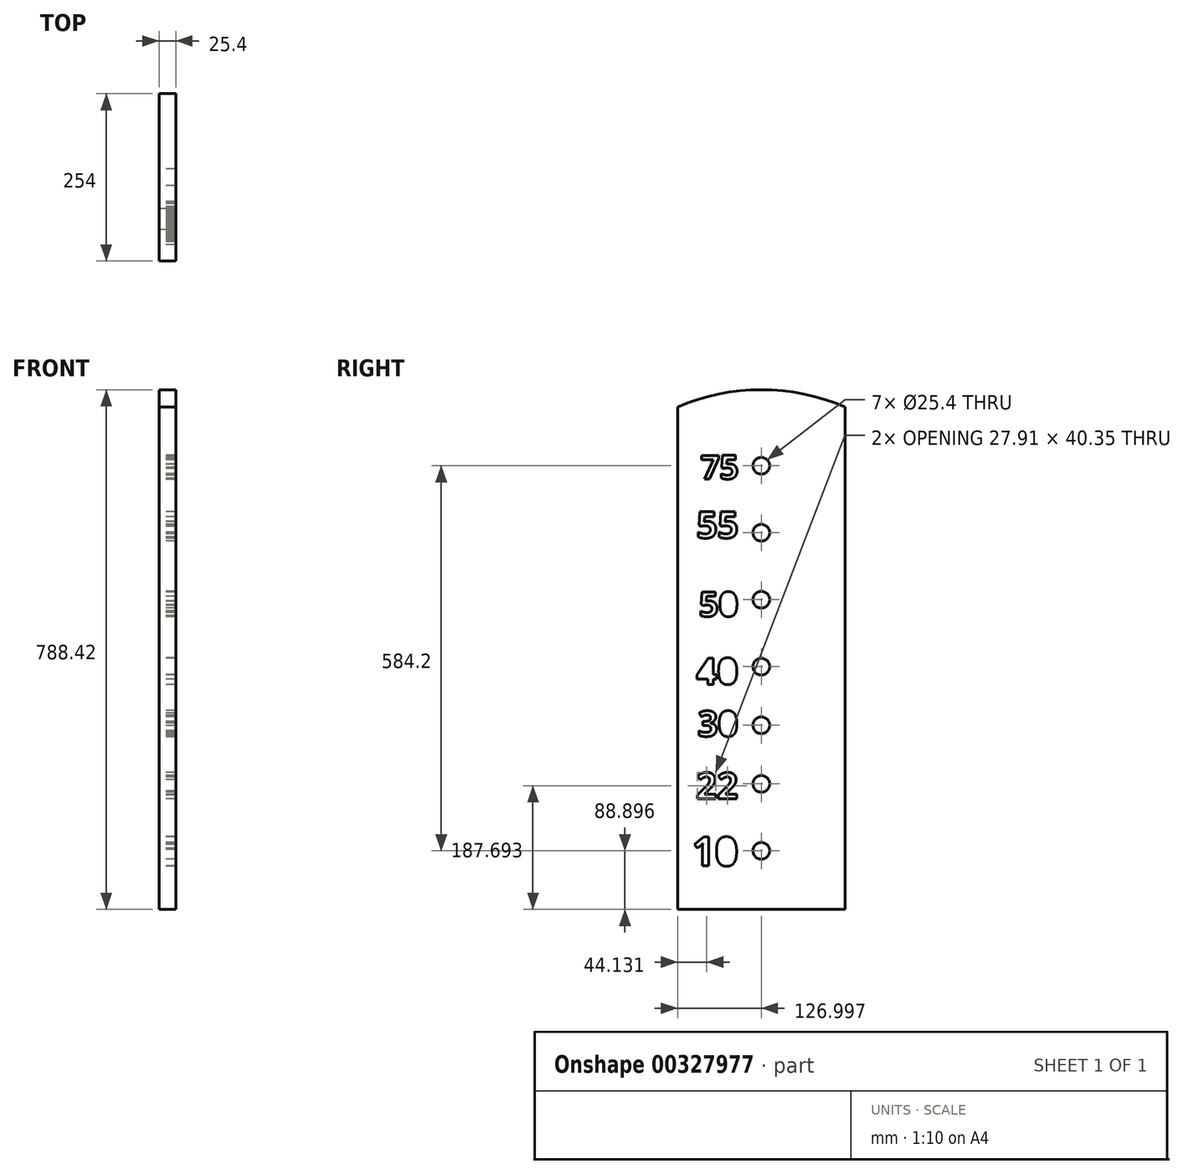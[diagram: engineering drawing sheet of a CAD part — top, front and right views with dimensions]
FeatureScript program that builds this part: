
annotation { "Feature Type Name" : "Feature", "Feature Type Description" : "" }
export const myFeature = defineFeature(function(context is Context, id is Id, definition is map)
    precondition{}
    {
        {
            var Q0;
            Q0=qCreatedBy(makeId("Right.planeOp"),FACE);
            var sketch = newSketch(context, id + "F0", { "sketchPlane" : qUnion([Q0])});
            skArc(sketch, "E0", {"start": v(-63.95, 233.67) * mm, "mid": v(-190.95, 260.09) * mm, "end": v(-317.95, 233.67) * mm});
            skLineSegment(sketch, "E1", {"start": v(-317.95, 233.67) * mm, "end": v(-317.95, -528.33) * mm});
            skLineSegment(sketch, "E2", {"start": v(-63.95, 233.67) * mm, "end": v(-63.95, -528.33) * mm});
            skLineSegment(sketch, "E3", {"start": v(-63.95, -528.33) * mm, "end": v(-317.95, -528.33) * mm});
            skCircle(sketch, "E4", {"center": v(-190.95, -439.43) * mm, "radius": 12.7 * mm});
            skPoint(sketch, "E4.centerSnap0", {"position": v(-190.95, -528.33) * mm});
            skCircle(sketch, "E5", {"center": v(-190.95, -337.83) * mm, "radius": 12.7 * mm});
            skCircle(sketch, "E6", {"center": v(-190.95, -248.93) * mm, "radius": 12.7 * mm});
            skCircle(sketch, "E7", {"center": v(-190.95, -160.03) * mm, "radius": 12.7 * mm});
            skCircle(sketch, "E8", {"center": v(-190.95, -58.43) * mm, "radius": 12.7 * mm});
            skCircle(sketch, "E9", {"center": v(-190.95, 43.17) * mm, "radius": 12.7 * mm});
            skCircle(sketch, "E10", {"center": v(-190.95, 144.77) * mm, "radius": 12.7 * mm});
            skText(sketch, "E11", { "text": "75", "fontName": "OpenSans-Bold.ttf"});
            skText(sketch, "E12", { "text": "55", "fontName": "OpenSans-Bold.ttf"});
            skPoint(sketch, "E12.secondSnap0", {"position": v(-224.45, 142.71) * mm});
            skText(sketch, "E13", { "text": "50", "fontName": "OpenSans-Bold.ttf"});
            skText(sketch, "E14", { "text": "40", "fontName": "OpenSans-Bold.ttf"});
            skText(sketch, "E15", { "text": "30", "fontName": "OpenSans-Bold.ttf"});
            skText(sketch, "E16", { "text": "22", "fontName": "OpenSans-Bold.ttf"});
            skText(sketch, "E17", { "text": "10", "fontName": "OpenSans-Bold.ttf"});
            const initialGuessF0  = {"E11": [-0.2827, 0.12466, 1, 0, 0.0361], "E12": [-0.28917, 0.03505, 1, 0, 0.04012], "E13": [-0.28537, -0.08397, 1, 0, 0.03745], "E14": [-0.28969, -0.18695, 1, 0, 0.04012], "E15": [-0.28751, -0.26586, 1, 0, 0.03878], "E16": [-0.2899, -0.36081, 1, 0, 0.04012], "E17": [-0.29621, -0.46245, 1, 0, 0.04413]};
            skSetInitialGuess(sketch, initialGuessF0);
            skSolve(sketch);
        }
        {
            var Q0;
            Q0=makeQuery(id+"F0.imprint","IMPRINT",FACE,{"disambiguationData":[TD([[makeQuery(id+"F0.imprint","IMPRINT",EDGE,{"derivedFrom":sQuery(id+"F0.wireOp",EDGE,"E0")}),1.0]])]});
            extrude(context, id + "F1", {"entities" : qUnion([Q0]), "depth" : 25.4 * mm});
        }
    });
